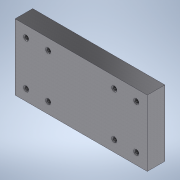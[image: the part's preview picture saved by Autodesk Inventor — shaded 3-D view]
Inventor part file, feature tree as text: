
AUTODESK INVENTOR PART (.ipt)
format: ipt  version: 2021 (Build 250183000, 183)  size: 139,776 bytes
history: native  units: mm
features: extrude x2, sketch x2, other x1, chamfer x1
ambient origin geometry x8: Origin, YZ Plane, XZ Plane, XY Plane, X Axis, Y Axis, Z Axis, Center Point
bodies: Body1 (feature_tree)
feature tree (6):
  other  "Sólido1"
  extrude  "Extrusão1"  Depth=300.0mm
  extrude  "Extrusão2"  Depth=40.0mm
  chamfer  "Chanfro1"  Distance=200.0mm
  sketch  "Esboço1"  dims[d0=600.0mm d1=300.0mm]
  sketch  "Esboço2"  dims[d2=80.0mm d3=0.0mm d4=500.0mm d5=200.0mm d6=300.0mm d7=16.0mm d8=16.0mm d9=16.0mm d10=16.0mm d11=16.0mm d12=16.0mm d13=16.0mm d14=16.0mm d15=40.0mm d16=0.0mm d17=4.0mm d18=2.0mm d19=45.0deg]
